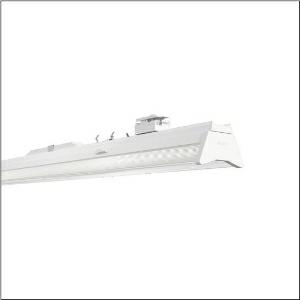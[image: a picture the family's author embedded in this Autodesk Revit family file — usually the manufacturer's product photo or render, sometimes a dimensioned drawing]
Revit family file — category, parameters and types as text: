
# Revit family: licross_r__11_performance_ho_51td16cn4exm_ed55
name_source: partatom
category: Lighting Fixtures
units: mm (PartAtom-declared; Revit-internal decimal feet)

## family parameters
Cut with Voids When Loaded = No
Host = Face
Light Source = No
Part Type = Normal
Room Calculation Point = No
Round Connector Dimension = Use Diameter
Shared = No

## types (1)
- --- (1 x LED, 14420 lm, 77.6 W, 4000K)
    Apparent Load = 78 VA
    CIE Flux Codes = 63 87 95 78 100
    Color Rendering = 80
    Color Temperature = 4000K
    Default Elevation = 1800 mm
    Description = Licross® 11 Performance HO, luminaire insert, of sheet steel, galvanised, coil coated, white, length: 1.500mm, width: 120mm, height: 123mm, LED rated luminous flux: 14.420lm, light colour: 840, control gear: ON/OFF Multilumen, CLOi, with plug, 3-pole, with phase selection, mains connection: 220..240V, AC, 50/60Hz, start of lifetime: 78W, end of service life: 87W, internal wiring halogen-free, primary light control with lens, of plastic, primary optical cover: cover, of PMMA, light emission: direct/indirect distribution, primary light characteristic: symmetric, protection rating (complete): IP54, insulation class (complete): insulation class I (protective earthing), certification: CE, ENEC, VDE, UKCA, protection symbol: D if used in an environment with non-conductive dust loads with corresponding accessories, impact resistance: IK06, permissible ambient temperature for indoor applications: -35..+35°C, corresponds to IFS (International Featured Standards) requirements for safety and quality in the food industry, reducing of maximum allowable ambient temperature of 5°C with ceiling mounting, LABS conformity tested according to VDMA 24364:2018-05, packaging unit: 1 piece
    Height = 114 mm
    Lamp = 1 x LED
    Lamp Light Flux = 14420 lm
    Lamp Power = 77.6 W
    Lamp count = 1
    Length = 1500 mm
    Luminous efficacy = 186 lm/W
    Manufacturer = Siteco
    ModVariant = No
    Model = 51TD16CN4EXM
    Mounting Place = Ceiling
    Mounting Type = Pendant
    Number of Poles = 1
    OnlyDefault = Yes
    Power Factor = 1
    Product Name = Licross® 11 Performance HO
    Product group = luminaire insert | ceiling pendant
    ProductGroupID = 902
    Protection Class = Protection class I
    Protection Degree = IP 54
    RLX_Detail_Level = 1
    RLX_Emergency_Light_Flux = 0 lm
    RLX_Emergency_Type = 0
    RLX_Emergency_Type_DB = No
    RlxData = <blob elided: 31913 chars, md5=2fdf6e5b>
    Socket = socket
    Standby Power = 0 W
    System Light Flux = 14420 lm
    System Power = 78 W
    Type Comments = factory setting: luminous flux: 100 % | (A | C | E) | 181 mA
    Type Image = l_1256138.jpg
    URL = http://relux.com
    VarID = @adj_107697
    Voltage = 0 V
    Weight = 0.00 kg
    Width = 120 mm

## geometry (parser evidence)
native form markers: Blend x4, Sweep x12
no freeform markers — native parametric forms only
